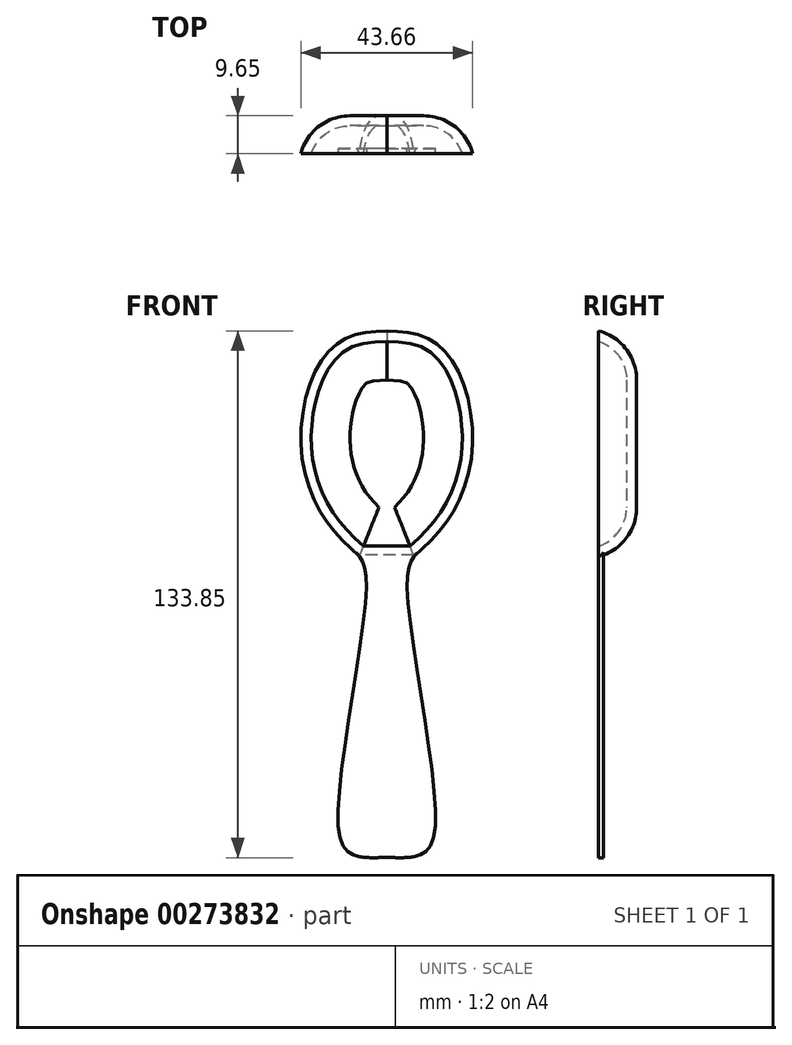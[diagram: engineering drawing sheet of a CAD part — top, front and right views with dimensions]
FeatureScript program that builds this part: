
annotation { "Feature Type Name" : "Feature", "Feature Type Description" : "" }
export const myFeature = defineFeature(function(context is Context, id is Id, definition is map)
    precondition{}
    {
        {
            var Q0;
            Q0=qCreatedBy(makeId("Front.planeOp"),FACE);
            var sketch = newSketch(context, id + "F0", { "sketchPlane" : qUnion([Q0])});
            skFitSpline(sketch, "E0", {"points": [v(0, -76.43) * mm, v(-8.6, -75.74) * mm, v(-12.4, -67.13) * mm, v(-5.16, -7.23) * mm, v(-6.89, 0) * mm], "startDerivative": vector(-53.58, -2.31) * mm, "endDerivative": vector(-15.9, 27.25) * mm});
            skLineSegment(sketch, "E1", {"start": v(0, -76.43) * mm, "end": v(0, 78.84) * mm, "construction": true});
            skFitSpline(sketch, "E2.MirrorCS", {"points": [v(0, -76.43) * mm, v(8.6, -75.74) * mm, v(12.4, -67.13) * mm, v(5.16, -7.23) * mm, v(6.89, 0) * mm], "startDerivative": vector(53.58, -2.31) * mm, "endDerivative": vector(15.9, 27.25) * mm});
            skLineSegment(sketch, "E3", {"start": v(-6.89, 0) * mm, "end": v(6.89, 0) * mm});
            skSolve(sketch);
        }
        {
            var Q0;
            Q0 = qSketchRegion(id + "F0", true);
            extrude(context, id + "F1", {"entities" : qUnion([Q0]), "oppositeDirection" : true, "depth" : 1.27 * mm});
        }
        {
            var Q0;
            Q0=qCreatedBy(makeId("Front.planeOp"),FACE);
            var sketch = newSketch(context, id + "F2", { "sketchPlane" : qUnion([Q0])});
            skFitSpline(sketch, "E4", {"points": [v(-6.95, 0) * mm, v(-15.92, 9.84) * mm, v(-21.71, 26.92) * mm, v(-18.24, 46.9) * mm, v(-10.13, 55.58) * mm, v(0, 57.32) * mm], "startDerivative": vector(-49.9, 46.15) * mm, "endDerivative": vector(62.93, 2.87) * mm});
            skFitSpline(sketch, "E5.MirrorCS", {"points": [v(6.95, 0) * mm, v(15.92, 9.84) * mm, v(21.71, 26.92) * mm, v(18.24, 46.9) * mm, v(10.13, 55.58) * mm, v(0, 57.32) * mm], "startDerivative": vector(49.9, 46.15) * mm, "endDerivative": vector(-62.93, 2.87) * mm});
            skLineSegment(sketch, "E6", {"start": v(-6.95, 0) * mm, "end": v(6.95, 0) * mm});
            skSolve(sketch);
        }
        {
            var Q0;
            Q0 = qSketchRegion(id + "F2", true);
            extrude(context, id + "F3", {"entities" : qUnion([Q0]), "operationType" : NewBodyOperationType.ADD, "oppositeDirection" : true, "depth" : 9.65 * mm});
        }
        {
            var Q0;
            Q0=makeQuery(id+"F3.opExtrude","CAP_FACE",FACE,{"disambiguationData":[OSD([sQuery(id+"F2.wireOp",EDGE,"E4"),sQuery(id+"F2.wireOp",EDGE,"E5.MirrorCS"),sQuery(id+"F2.wireOp",EDGE,"E6")])],"isStart":false});
            fillet(context, id + "F4", {"entities" : qUnion([Q0]), "radius" : 12.88 * mm, "tangentPropagation" : true, "allowEdgeOverflow" : false});
        }
        {
            var Q0;
            Q0=makeQuery(id+"F3.boolean.opBoolean","MERGE",FACE,{"derivedFrom":[makeQuery(id+"F1.opExtrude","CAP_FACE",FACE,{"disambiguationData":[OSD([sQuery(id+"F0.wireOp",EDGE,"E0"),sQuery(id+"F0.wireOp",EDGE,"E2.MirrorCS"),sQuery(id+"F0.wireOp",EDGE,"E3")])],"isStart":true}),makeQuery(id+"F3.opExtrude","CAP_FACE",FACE,{"disambiguationData":[OSD([sQuery(id+"F2.wireOp",EDGE,"E4"),sQuery(id+"F2.wireOp",EDGE,"E5.MirrorCS"),sQuery(id+"F2.wireOp",EDGE,"E6")])],"isStart":true})]});
            shell(context, id + "F5", {"entities" : qUnion([Q0]), "thickness" : 2.54 * mm});
        }
    });
